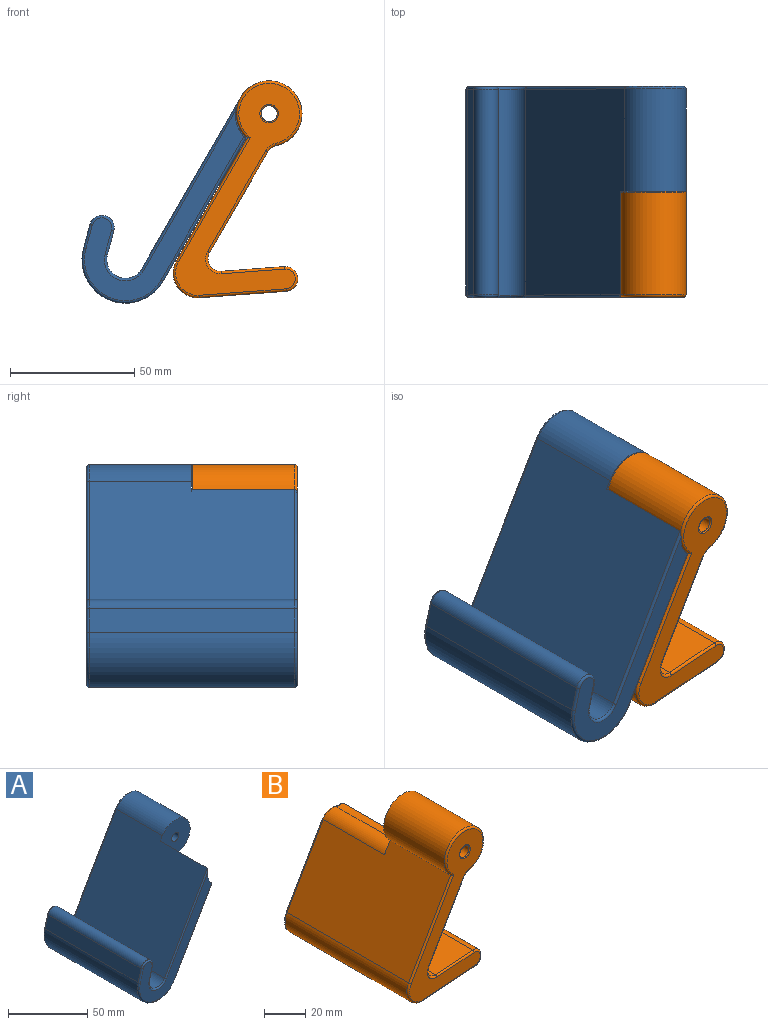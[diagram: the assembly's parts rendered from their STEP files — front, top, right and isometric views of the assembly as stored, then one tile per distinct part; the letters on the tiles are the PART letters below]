
ASSEMBLY  parts=2 mates=1
PART A: 39 faces, bbox 91.3x85x92.2 mm
  f0: cylinder r=3.25mm len=35.25mm, axis (0,1,0), area 719.8mm2, adj f13,f22
  f1: plane 87.66x86.72mm, normal (0,1,0), area 1281.8mm2, adj f14,f15,f16,f17,f18,f19,f20,f21
  f2: cylinder r=8mm len=41.25mm, axis (0,1,0), area 444mm2, adj f3,f9,f13,f32
  f3: cylinder r=13.25mm len=41.25mm, axis (0,1,0), area 2452.4mm2, adj f2,f10,f13,f30
  f4: cylinder r=7.5mm len=83mm, axis (0,1,0), area 1792.7mm2, adj f5,f10,f24,f33
  f5: plane 83x9.66mm, normal (0.97,0,-0.26), area 830mm2, adj f4,f6,f25,f35
  f6: cylinder r=5mm len=83mm, axis (0,1,0), area 1303.8mm2, adj f5,f7,f26,f37
  f7: plane 83x9.66mm, normal (-0.97,0,0.26), area 830mm2, adj f6,f8,f27,f38
  f8: cylinder r=17.5mm len=83mm, axis (0,1,0), area 4182.9mm2, adj f7,f9,f28,f36
  f9: plane 83x57.71mm, normal (0.87,0,-0.5), area 5227.8mm2, adj f2,f8,f12,f13,f29,f34
  f10: plane 83x69.28mm, normal (-0.87,0,0.5), area 6486.6mm2, adj f3,f4,f12,f13,f23,f31
  f11: plane 76.12x64.25mm, normal (0,-1,0), area 948.4mm2, adj f12,f23,f24,f25,f26,f27,f28,f29
  f12: cylinder r=13.75mm len=42.75mm, axis (0,1,0), area 623.2mm2, adj f9,f10,f11,f13,f23,f29
  f13: plane 29.56x27mm, normal (0,-1,0), area 537.1mm2, adj f0,f2,f3,f9,f10,f12
  f14: plane 9.61x7mm, normal (0.5,0,0.87), area 77.7mm2, adj f1,f15,f21,f22
  f15: cylinder r=1mm len=7mm, axis (0,1,0), area 11mm2, adj f1,f14,f16,f22
  f16: plane 9.61x7mm, normal (0.87,0,-0.5), area 77.7mm2, adj f1,f15,f17,f22
  f17: cylinder r=1mm len=7mm, axis (0,1,0), area 11mm2, adj f1,f16,f18,f22
  f18: plane 9.61x7mm, normal (-0.5,0,-0.87), area 77.7mm2, adj f1,f17,f19,f22
  f19: cylinder r=1mm len=7mm, axis (0,1,0), area 11mm2, adj f1,f18,f20,f22
  f20: plane 9.61x7mm, normal (-0.87,0,0.5), area 77.7mm2, adj f1,f19,f21,f22
  f21: cylinder r=1mm len=7mm, axis (0,1,0), area 11mm2, adj f1,f14,f20,f22
  f22: plane 17.16x17.16mm, normal (0,1,0), area 137.6mm2, adj f0,f14,f15,f16,f17,f18,f19,f20
  f23: cylinder r=1mm len=66.6mm, axis (0.5,0,0.87), area 118.3mm2, adj f10,f11,f12,f24
  f24: torus R=8.5mm, axis (0,-1,0), area 35.6mm2, adj f4,f11,f23,f25
  f25: cylinder r=1mm len=9.92mm, axis (-0.26,0,-0.97), area 15.7mm2, adj f5,f11,f24,f26
  f26: torus R=4mm, axis (0,-1,0), area 22.9mm2, adj f6,f11,f25,f27
  f27: cylinder r=1mm len=9.92mm, axis (0.26,0,0.97), area 15.7mm2, adj f7,f11,f26,f28
  f28: torus R=16.5mm, axis (0,-1,0), area 77.5mm2, adj f8,f11,f27,f29
  f29: cylinder r=1mm len=58.46mm, axis (-0.5,0,-0.87), area 104.8mm2, adj f9,f11,f12,f28
  f30: torus R=12.25mm, axis (0,1,0), area 90.8mm2, adj f1,f3,f31,f32
  f31: cylinder r=1mm len=69.78mm, axis (0.5,0,0.87), area 125.7mm2, adj f1,f10,f30,f33
  f32: torus R=9mm, axis (0,1,0), area 17.7mm2, adj f1,f2,f30,f34
  f33: torus R=8.5mm, axis (0,1,0), area 35.6mm2, adj f1,f4,f31,f35
  f34: cylinder r=1mm len=51.84mm, axis (-0.5,0,-0.87), area 93.1mm2, adj f1,f9,f32,f36
  f35: cylinder r=1mm len=9.92mm, axis (-0.26,0,-0.97), area 15.7mm2, adj f1,f5,f33,f37
  f36: torus R=16.5mm, axis (0,1,0), area 77.5mm2, adj f1,f8,f34,f38
  f37: torus R=4mm, axis (0,1,0), area 22.9mm2, adj f1,f6,f35,f38
  f38: cylinder r=1mm len=9.92mm, axis (0.26,0,0.97), area 15.7mm2, adj f1,f7,f36,f37
PART B: 35 faces, bbox 53.9x85x89.4 mm
  f0: plane 85.5x49.97mm, normal (0,-1,0), area 1314.1mm2, adj f25,f26,f27,f28,f29,f30,f31,f32
  f1: plane 83x34.9mm, normal (0.07,0,-1), area 2905mm2, adj f2,f9,f16,f29
  f2: cylinder r=5mm len=83mm, axis (0,1,0), area 1303.8mm2, adj f1,f3,f15,f27
  f3: plane 83x25.47mm, normal (-0.07,0,1), area 2120.1mm2, adj f2,f4,f17,f25
  f4: cylinder r=5mm len=83mm, axis (0,1,0), area 900.1mm2, adj f3,f5,f19,f26
  f5: plane 83x40.72mm, normal (0.87,0,-0.5), area 3902.3mm2, adj f4,f6,f21,f28
  f6: cylinder r=5mm len=83mm, axis (0,1,0), area 265.7mm2, adj f5,f7,f8,f14,f23,f30
  f7: plane 29.81x26.5mm, normal (0,1,0), area 533.5mm2, adj f6,f8,f10,f11,f13,f14
  f8: cylinder r=13.25mm len=41.25mm, axis (0,1,0), area 2917.7mm2, adj f6,f7,f10,f32
  f9: cylinder r=10mm len=83mm, axis (0,1,0), area 1800.1mm2, adj f1,f10,f18,f31
  f10: plane 83x49.4mm, normal (-0.87,0,0.5), area 4410.6mm2, adj f7,f8,f9,f13,f20,f33
  f11: cylinder r=3.25mm len=41.75mm, axis (0,1,0), area 852.5mm2, adj f7,f34
  f12: plane 59.43x48.28mm, normal (0,1,0), area 858.3mm2, adj f15,f16,f17,f18,f19,f20,f21,f22
  f13: cylinder r=7.5mm len=41.75mm, axis (0,-1,0), area 421.3mm2, adj f7,f10,f14,f22
  f14: cylinder r=13.75mm len=41.75mm, axis (0,-1,0), area 214mm2, adj f6,f7,f13,f24
  f15: torus R=4mm, axis (0,1,0), area 22.9mm2, adj f2,f12,f16,f17
  f16: cylinder r=1mm len=34.98mm, axis (-1,0,-0.07), area 55mm2, adj f1,f12,f15,f18
  f17: cylinder r=1mm len=25.55mm, axis (1,0,0.07), area 40.1mm2, adj f3,f12,f15,f19
  f18: torus R=9mm, axis (0,1,0), area 32.8mm2, adj f9,f12,f16,f20
  f19: torus R=6mm, axis (0,1,0), area 18.3mm2, adj f4,f12,f17,f21
  f20: cylinder r=1mm len=43.18mm, axis (0.5,0,0.87), area 77.4mm2, adj f10,f12,f18,f22
  f21: cylinder r=1mm len=41.22mm, axis (-0.5,0,-0.87), area 73.9mm2, adj f5,f12,f19,f23
  f22: torus R=6.5mm, axis (0,1,0), area 15.1mm2, adj f12,f13,f20,f24
  f23: torus R=6mm, axis (0,1,0), area 2.2mm2, adj f6,f12,f21,f24
  f24: torus R=14.75mm, axis (0,1,0), area 6.7mm2, adj f12,f14,f22,f23
  f25: cylinder r=1mm len=25.55mm, axis (1,0,0.07), area 40.1mm2, adj f0,f3,f26,f27
  f26: torus R=6mm, axis (0,-1,0), area 18.3mm2, adj f0,f4,f25,f28
  f27: torus R=4mm, axis (0,-1,0), area 22.9mm2, adj f0,f2,f25,f29
  f28: cylinder r=1mm len=41.22mm, axis (-0.5,0,-0.87), area 73.9mm2, adj f0,f5,f26,f30
  f29: cylinder r=1mm len=34.98mm, axis (-1,0,-0.07), area 55mm2, adj f0,f1,f27,f31
  f30: torus R=6mm, axis (0,-1,0), area 7mm2, adj f0,f6,f28,f32
  f31: torus R=9mm, axis (0,-1,0), area 32.8mm2, adj f0,f9,f29,f33
  f32: torus R=12.25mm, axis (0,-1,0), area 108.5mm2, adj f0,f8,f30,f33
  f33: cylinder r=1mm len=50.62mm, axis (0.5,0,0.87), area 90.1mm2, adj f0,f10,f31,f32
  f34: torus R=3.75mm, axis (0,-1,0), area 16.9mm2, adj f0,f11
PLACE A t=(-49.91,3.59,-1.03)mm
PLACE B t=(-49.91,3.59,-1.03)mm
MATE revolute A.f0 <-> B.f8  axis (0,1,0) through (8.06,3.84,57.88)mm
